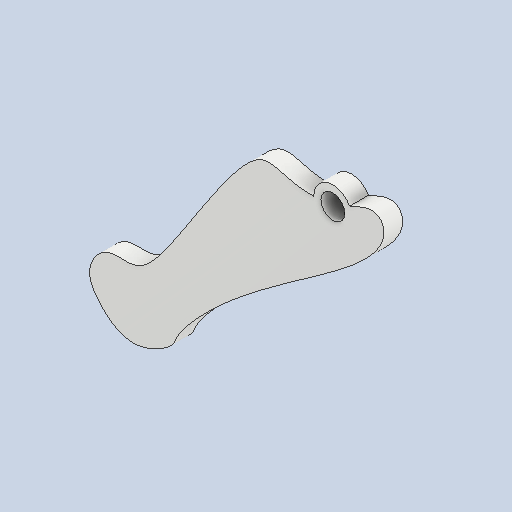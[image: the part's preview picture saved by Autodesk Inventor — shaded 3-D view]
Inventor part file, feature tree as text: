
AUTODESK INVENTOR PART (.ipt)
format: ipt  version: 2022 (Build 260153000, 153)  size: 111,616 bytes
history: native  units: in
note: dims shown in document units (in); Inventor stores cm internally (conversion verified against a paired STEP export)
features: other x3, sketch x1
ambient origin geometry x8: Origin, YZ Plane, XZ Plane, XY Plane, X Axis, Y Axis, Z Axis, Center Point
bodies: Solid1 (feature_tree)
feature tree (4):
  other  "Component36.ipt"
  other  "Solid1::Component36.ipt"
  other  "TaggingFeature1"
  sketch  "Sketch2"  dims[d0=0.3937in]
